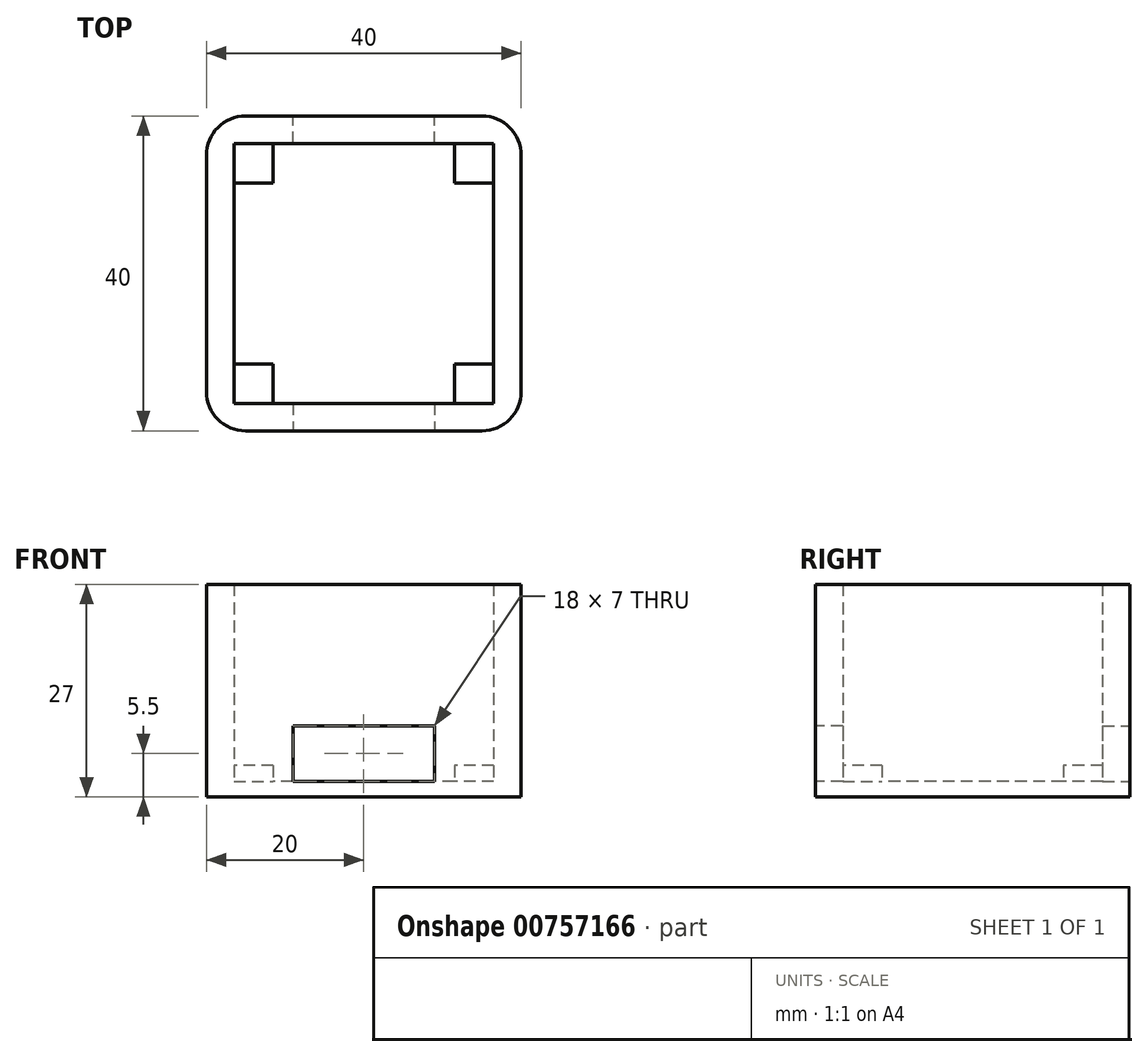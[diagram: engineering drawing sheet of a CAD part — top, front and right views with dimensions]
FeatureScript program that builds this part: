
annotation { "Feature Type Name" : "Feature", "Feature Type Description" : "" }
export const myFeature = defineFeature(function(context is Context, id is Id, definition is map)
    precondition{}
    {
        {
            var Q0;
            Q0=qCreatedBy(makeId("Top.planeOp"),FACE);
            var sketch = newSketch(context, id + "F0", { "sketchPlane" : qUnion([Q0])});
            skLineSegment(sketch, "E0.bottom", {"start": v(16.5, 16.5) * mm, "end": v(-16.5, 16.5) * mm});
            skLineSegment(sketch, "E0.top", {"start": v(16.5, -16.5) * mm, "end": v(-16.5, -16.5) * mm});
            skLineSegment(sketch, "E0.left", {"start": v(16.5, 16.5) * mm, "end": v(16.5, -16.5) * mm});
            skLineSegment(sketch, "E0.right", {"start": v(-16.5, 16.5) * mm, "end": v(-16.5, -16.5) * mm});
            skPoint(sketch, "E0.middle", {"position": v(0, 0) * mm});
            skLineSegment(sketch, "E1.bottom", {"start": v(20, 20) * mm, "end": v(-20, 20) * mm});
            skLineSegment(sketch, "E1.top", {"start": v(20, -20) * mm, "end": v(-20, -20) * mm});
            skLineSegment(sketch, "E1.left", {"start": v(20, 20) * mm, "end": v(20, -20) * mm});
            skLineSegment(sketch, "E1.right", {"start": v(-20, 20) * mm, "end": v(-20, -20) * mm});
            skSolve(sketch);
        }
        {
            var Q0;
            Q0 = qSketchRegion(id + "F0", true);
            extrude(context, id + "F1", {"entities" : qUnion([Q0]), "depth" : 25 * mm, "offsetDistance" : 25 * mm});
        }
        {
            var Q0;
            Q0=qCreatedBy(makeId("Top.planeOp"),FACE);
            var sketch = newSketch(context, id + "F2", { "sketchPlane" : qUnion([Q0])});
            skLineSegment(sketch, "E2.bottom", {"start": v(20, -20) * mm, "end": v(-20, -20) * mm});
            skLineSegment(sketch, "E2.top", {"start": v(20, 20) * mm, "end": v(-20, 20) * mm});
            skLineSegment(sketch, "E2.left", {"start": v(20, -20) * mm, "end": v(20, 20) * mm});
            skLineSegment(sketch, "E2.right", {"start": v(-20, -20) * mm, "end": v(-20, 20) * mm});
            skPoint(sketch, "E2.middle", {"position": v(0, 0) * mm});
            skSolve(sketch);
        }
        {
            var Q0;
            Q0 = qSketchRegion(id + "F2", true);
            extrude(context, id + "F3", {"entities" : qUnion([Q0]), "operationType" : NewBodyOperationType.ADD, "oppositeDirection" : true, "depth" : 2 * mm, "offsetDistance" : 25 * mm});
        }
        {
            var Q0;
            Q0=makeQuery(id+"F3.opExtrude","CAP_FACE",FACE,{"disambiguationData":[OSD([sQuery(id+"F2.wireOp",EDGE,"E2.bottom"),sQuery(id+"F2.wireOp",EDGE,"E2.top"),sQuery(id+"F2.wireOp",EDGE,"E2.left"),sQuery(id+"F2.wireOp",EDGE,"E2.right")])],"isStart":true});
            var sketch = newSketch(context, id + "F4", { "sketchPlane" : qUnion([Q0])});
            skLineSegment(sketch, "E3.bottom", {"start": v(-16.5, 16.5) * mm, "end": v(-11.5, 16.5) * mm});
            skLineSegment(sketch, "E3.top", {"start": v(-16.5, 11.5) * mm, "end": v(-11.5, 11.5) * mm});
            skLineSegment(sketch, "E3.left", {"start": v(-16.5, 16.5) * mm, "end": v(-16.5, 11.5) * mm});
            skLineSegment(sketch, "E3.right", {"start": v(-11.5, 16.5) * mm, "end": v(-11.5, 11.5) * mm});
            skLineSegment(sketch, "E4.bottom", {"start": v(16.5, 16.5) * mm, "end": v(11.5, 16.5) * mm});
            skLineSegment(sketch, "E4.top", {"start": v(16.5, 11.5) * mm, "end": v(11.5, 11.5) * mm});
            skLineSegment(sketch, "E4.left", {"start": v(16.5, 16.5) * mm, "end": v(16.5, 11.5) * mm});
            skLineSegment(sketch, "E4.right", {"start": v(11.5, 16.5) * mm, "end": v(11.5, 11.5) * mm});
            skLineSegment(sketch, "E5.bottom", {"start": v(-16.5, -16.5) * mm, "end": v(-11.5, -16.5) * mm});
            skLineSegment(sketch, "E5.top", {"start": v(-16.5, -11.5) * mm, "end": v(-11.5, -11.5) * mm});
            skLineSegment(sketch, "E5.left", {"start": v(-16.5, -16.5) * mm, "end": v(-16.5, -11.5) * mm});
            skLineSegment(sketch, "E5.right", {"start": v(-11.5, -16.5) * mm, "end": v(-11.5, -11.5) * mm});
            skLineSegment(sketch, "E6.bottom", {"start": v(16.5, -16.5) * mm, "end": v(11.5, -16.5) * mm});
            skLineSegment(sketch, "E6.top", {"start": v(16.5, -11.5) * mm, "end": v(11.5, -11.5) * mm});
            skLineSegment(sketch, "E6.left", {"start": v(16.5, -16.5) * mm, "end": v(16.5, -11.5) * mm});
            skLineSegment(sketch, "E6.right", {"start": v(11.5, -16.5) * mm, "end": v(11.5, -11.5) * mm});
            skSolve(sketch);
        }
        {
            var Q0;
            Q0 = qSketchRegion(id + "F4", true);
            extrude(context, id + "F5", {"entities" : qUnion([Q0]), "operationType" : NewBodyOperationType.ADD, "depth" : 2 * mm, "offsetDistance" : 25 * mm});
        }
        {
            var Q0;
            Q0=makeQuery(id+"F3.opExtrude","CAP_FACE",FACE,{"disambiguationData":[OSD([sQuery(id+"F2.wireOp",EDGE,"E2.bottom"),sQuery(id+"F2.wireOp",EDGE,"E2.top"),sQuery(id+"F2.wireOp",EDGE,"E2.left"),sQuery(id+"F2.wireOp",EDGE,"E2.right")])],"isStart":true});
            var sketch = newSketch(context, id + "F6", { "sketchPlane" : qUnion([Q0])});
            skLineSegment(sketch, "E7.bottom", {"start": v(-9, -16.5) * mm, "end": v(9, -16.5) * mm});
            skLineSegment(sketch, "E7.top", {"start": v(-9, -20) * mm, "end": v(9, -20) * mm});
            skLineSegment(sketch, "E7.left", {"start": v(-9, -16.5) * mm, "end": v(-9, -20) * mm});
            skLineSegment(sketch, "E7.right", {"start": v(9, -16.5) * mm, "end": v(9, -20) * mm});
            skLineSegment(sketch, "E8.MirrorCS", {"start": v(-9, 16.5) * mm, "end": v(9, 16.5) * mm});
            skLineSegment(sketch, "E9.MirrorCS", {"start": v(-9, 20) * mm, "end": v(9, 20) * mm});
            skLineSegment(sketch, "E10.MirrorCS", {"start": v(9, 16.5) * mm, "end": v(9, 20) * mm});
            skLineSegment(sketch, "E11.MirrorCS", {"start": v(-9, 16.5) * mm, "end": v(-9, 20) * mm});
            skSolve(sketch);
        }
        {
            var Q0;
            Q0 = qSketchRegion(id + "F6", true);
            extrude(context, id + "F7", {"entities" : qUnion([Q0]), "operationType" : NewBodyOperationType.REMOVE, "depth" : 7 * mm, "offsetDistance" : 25 * mm});
        }
        {
            var Q0;
            Q0=makeQuery(id+"F3.boolean.opBoolean","MERGE",EDGE,{"derivedFrom":[makeQuery(id+"F1.opExtrude","SWEPT_EDGE",EDGE,{"disambiguationData":[OSD([sQuery(id+"F0.wireOp",EDGE,"E1.top"),sQuery(id+"F0.wireOp",EDGE,"E1.left")])]}),makeQuery(id+"F3.opExtrude","SWEPT_EDGE",EDGE,{"disambiguationData":[OSD([sQuery(id+"F2.wireOp",EDGE,"E2.bottom"),sQuery(id+"F2.wireOp",EDGE,"E2.left")])]})]});
            var Q1;
            Q1=makeQuery(id+"F3.boolean.opBoolean","MERGE",EDGE,{"derivedFrom":[makeQuery(id+"F1.opExtrude","SWEPT_EDGE",EDGE,{"disambiguationData":[OSD([sQuery(id+"F0.wireOp",EDGE,"E1.top"),sQuery(id+"F0.wireOp",EDGE,"E1.right")])]}),makeQuery(id+"F3.opExtrude","SWEPT_EDGE",EDGE,{"disambiguationData":[OSD([sQuery(id+"F2.wireOp",EDGE,"E2.bottom"),sQuery(id+"F2.wireOp",EDGE,"E2.right")])]})]});
            var Q2;
            Q2=makeQuery(id+"F3.boolean.opBoolean","MERGE",EDGE,{"derivedFrom":[makeQuery(id+"F1.opExtrude","SWEPT_EDGE",EDGE,{"disambiguationData":[OSD([sQuery(id+"F0.wireOp",EDGE,"E1.bottom"),sQuery(id+"F0.wireOp",EDGE,"E1.left")])]}),makeQuery(id+"F3.opExtrude","SWEPT_EDGE",EDGE,{"disambiguationData":[OSD([sQuery(id+"F2.wireOp",EDGE,"E2.top"),sQuery(id+"F2.wireOp",EDGE,"E2.left")])]})]});
            var Q3;
            Q3=makeQuery(id+"F3.boolean.opBoolean","MERGE",EDGE,{"derivedFrom":[makeQuery(id+"F1.opExtrude","SWEPT_EDGE",EDGE,{"disambiguationData":[OSD([sQuery(id+"F0.wireOp",EDGE,"E1.bottom"),sQuery(id+"F0.wireOp",EDGE,"E1.right")])]}),makeQuery(id+"F3.opExtrude","SWEPT_EDGE",EDGE,{"disambiguationData":[OSD([sQuery(id+"F2.wireOp",EDGE,"E2.top"),sQuery(id+"F2.wireOp",EDGE,"E2.right")])]})]});
            fillet(context, id + "F8", {"entities" : qUnion([Q0, Q1, Q2, Q3]), "radius" : 5 * mm, "tangentPropagation" : true, "allowEdgeOverflow" : false});
        }
    });
